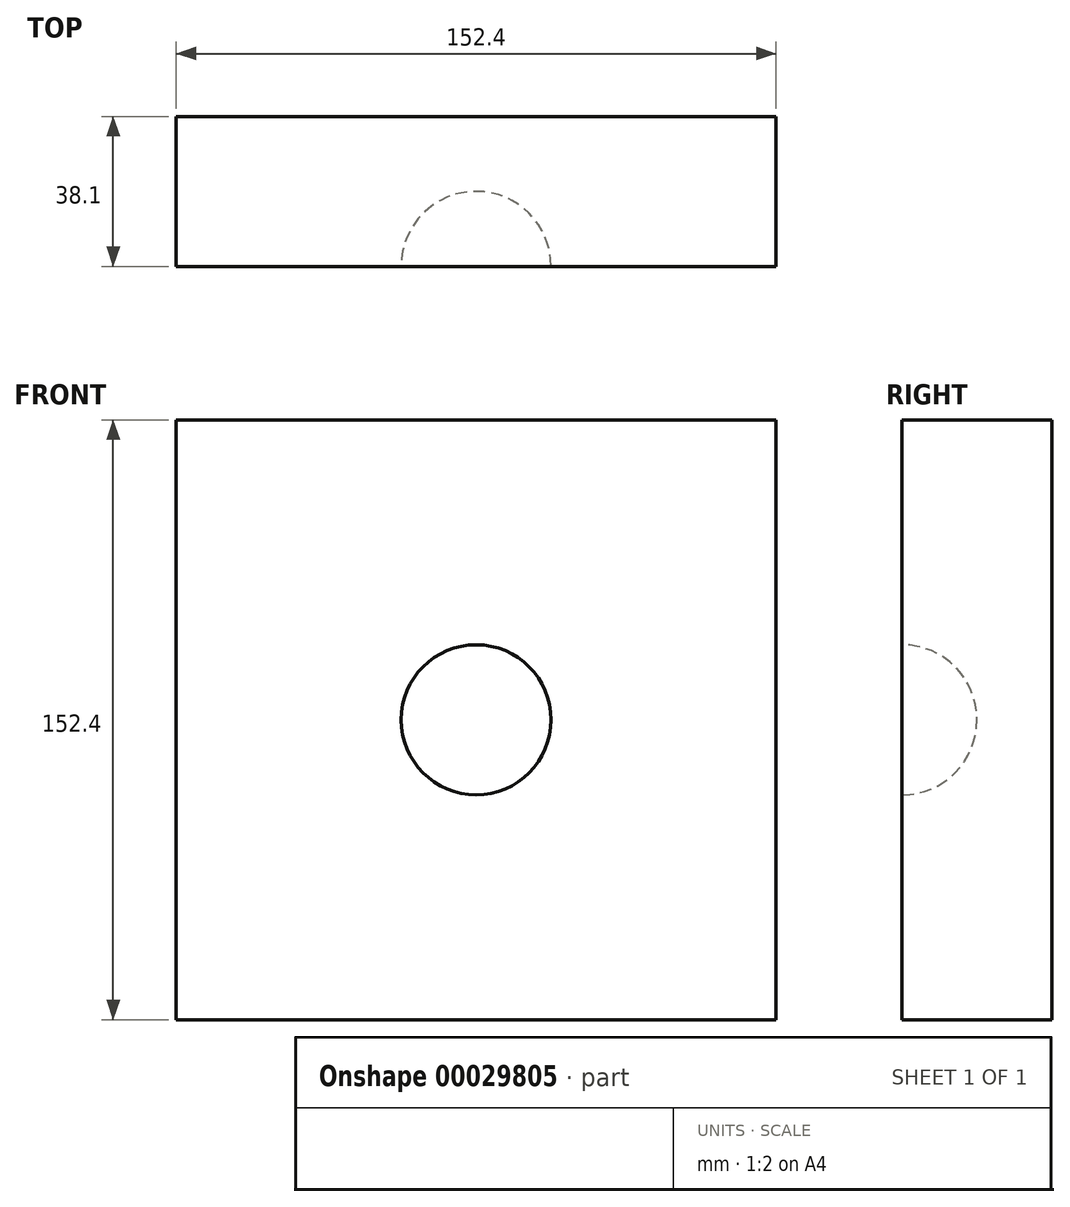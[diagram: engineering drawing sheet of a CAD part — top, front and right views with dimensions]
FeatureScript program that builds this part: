
annotation { "Feature Type Name" : "Feature", "Feature Type Description" : "" }
export const myFeature = defineFeature(function(context is Context, id is Id, definition is map)
    precondition{}
    {
        {
            var Q0;
            Q0=qCreatedBy(makeId("Front.planeOp"),FACE);
            var sketch = newSketch(context, id + "F0", { "sketchPlane" : qUnion([Q0])});
            skLineSegment(sketch, "E0.rect.bottom", {"start": v(76.2, -76.2) * mm, "end": v(-76.2, -76.2) * mm});
            skLineSegment(sketch, "E0.rect.top", {"start": v(76.2, 76.2) * mm, "end": v(-76.2, 76.2) * mm});
            skLineSegment(sketch, "E0.rect.left", {"start": v(76.2, -76.2) * mm, "end": v(76.2, 76.2) * mm});
            skLineSegment(sketch, "E0.rect.right", {"start": v(-76.2, -76.2) * mm, "end": v(-76.2, 76.2) * mm});
            skPoint(sketch, "E0.rect.middle", {"position": v(0, 0) * mm});
            skSolve(sketch);
        }
        {
            var Q0;
            Q0=makeQuery(id+"F0.imprint","IMPRINT",FACE,{"disambiguationData":[TD([[makeQuery(id+"F0.imprint","IMPRINT",EDGE,{"derivedFrom":sQuery(id+"F0.wireOp",EDGE,"E0.rect.bottom")}),-1.0]])]});
            extrude(context, id + "F1", {"entities" : qUnion([Q0]), "depth" : 38.1 * mm});
        }
        {
            var Q0;
            Q0=makeQuery(id+"F1.opExtrude","CAP_FACE",FACE,{"disambiguationData":[OSD([sQuery(id+"F0.wireOp",EDGE,"E0.rect.bottom"),sQuery(id+"F0.wireOp",EDGE,"E0.rect.top"),sQuery(id+"F0.wireOp",EDGE,"E0.rect.left"),sQuery(id+"F0.wireOp",EDGE,"E0.rect.right")])],"isStart":false});
            var sketch = newSketch(context, id + "F2", { "sketchPlane" : qUnion([Q0])});
            skCircle(sketch, "E1", {"center": v(0, 0) * mm, "radius": 19.05 * mm});
            skLineSegment(sketch, "E2", {"start": v(0, 19.05) * mm, "end": v(0, -19.05) * mm});
            skSolve(sketch);
        }
        {
            var Q0;
            {var subQ0=sQuery(id+"F2.wireOp",EDGE,"E2");Q0=makeQuery(id+"F2.imprint","IMPRINT",FACE,{"disambiguationData":[TD([[makeQuery(id+"F2.imprint","IMPRINT",EDGE,{"derivedFrom":subQ0}),-1.0]])]});}
            var Q1;
            Q1=sQuery(id+"F2.wireOp",EDGE,"E2");
            revolve(context, id + "F3", {"operationType" : NewBodyOperationType.REMOVE, "entities" : qUnion([Q0]), "axis" : qUnion([Q1]), "revolveType" : RevolveType.FULL, "oppositeDirection" : true});
        }
    });
